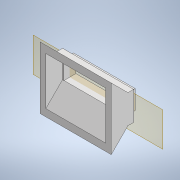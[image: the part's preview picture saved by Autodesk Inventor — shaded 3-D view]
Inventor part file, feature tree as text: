
AUTODESK INVENTOR PART (.ipt)
format: ipt  version: 2022 (Build 260153000, 153)  size: 158,720 bytes
history: native  units: mm
features: extrude x4, sketch x4, projected_geometry x3, other x3, reference x2, plane x1, mirror x1
ambient origin geometry x8: Origin, YZ Plane, XZ Plane, XY Plane, X Axis, Y Axis, Z Axis, Center Point
bodies: Solid1 (feature_tree)
feature tree (18):
  extrude  "Extrusion1"  Depth=0.1mm
  plane  "Work Plane1"
  extrude  "Extrusion2"  Depth=0.1mm
  extrude  "Extrusion3"  Depth=5.0mm TaperAngle=0.0deg
  extrude  "Extrusion4"  Depth=5.0mm TaperAngle=0.0deg
  mirror  "Mirror1"
  sketch  "Sketch1"  dims[d0=0.1mm d1=0.1mm]
  reference  "Reference1"
  reference  "Reference2"
  sketch  "Sketch2"  dims[d2=0.1mm d3=0.1mm]
  projected_geometry  "Projected Loop1"
  sketch  "Sketch3"  dims[d4=1.0mm d5=5.0mm d6=0.0mm]
  sketch  "Sketch4"  dims[d7=2.0mm d8=5.0mm d9=0.0mm d10=20.0mm d11=45.0deg d12=25.0mm d13=0.0mm d14=24.0mm d15=0.0mm]
  projected_geometry  "Projected Loop2"
  projected_geometry  "Projected Loop3"
  other  "Solids Feeder Head Assembly.iam"
  other  "body:1"
  other  "body cover:1"
